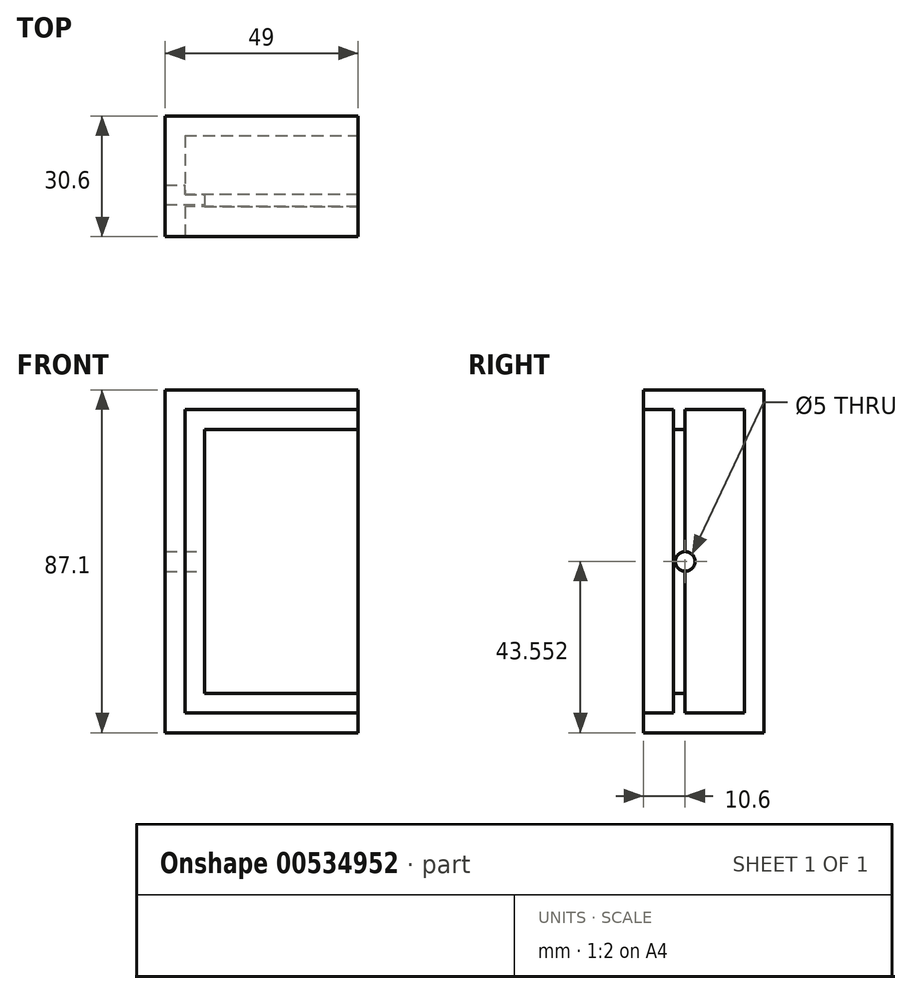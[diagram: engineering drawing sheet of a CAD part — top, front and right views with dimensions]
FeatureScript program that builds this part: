
annotation { "Feature Type Name" : "Feature", "Feature Type Description" : "" }
export const myFeature = defineFeature(function(context is Context, id is Id, definition is map)
    precondition{}
    {
        {
            var Q0;
            Q0=qCreatedBy(makeId("Front.planeOp"),FACE);
            var sketch = newSketch(context, id + "F0", { "sketchPlane" : qUnion([Q0])});
            skLineSegment(sketch, "E0.bottom", {"start": v(-22.43, 61.47) * mm, "end": v(21.57, 61.47) * mm});
            skLineSegment(sketch, "E0.top", {"start": v(-22.43, -15.63) * mm, "end": v(21.57, -15.63) * mm});
            skLineSegment(sketch, "E0.left", {"start": v(-22.43, 61.47) * mm, "end": v(-22.43, -15.63) * mm});
            skLineSegment(sketch, "E0.right", {"start": v(21.57, 61.47) * mm, "end": v(21.57, -15.63) * mm});
            skSolve(sketch);
        }
        {
            var Q0;
            Q0 = qSketchRegion(id + "F0", true);
            extrude(context, id + "F1", {"entities" : qUnion([Q0]), "depth" : 5 * mm, "offsetDistance" : 25.4 * mm});
        }
        {
            var Q0;
            Q0=makeQuery(id+"F1.opExtrude","SWEPT_FACE",FACE,{"disambiguationData":[OSD([sQuery(id+"F0.wireOp",EDGE,"E0.left")])]});
            var sketch = newSketch(context, id + "F2", { "sketchPlane" : qUnion([Q0])});
            skLineSegment(sketch, "E1.bottom", {"start": v(0, 61.47) * mm, "end": v(27.6, 61.47) * mm});
            skLineSegment(sketch, "E1.top", {"start": v(0, -15.63) * mm, "end": v(27.6, -15.63) * mm});
            skLineSegment(sketch, "E1.left", {"start": v(0, 61.47) * mm, "end": v(0, -15.63) * mm});
            skLineSegment(sketch, "E1.right", {"start": v(27.6, 61.47) * mm, "end": v(27.6, -15.63) * mm});
            skSolve(sketch);
        }
        {
            var Q0;
            Q0 = qSketchRegion(id + "F2", true);
            extrude(context, id + "F3", {"entities" : qUnion([Q0]), "operationType" : NewBodyOperationType.ADD, "depth" : 5 * mm, "offsetDistance" : 25.4 * mm});
        }
        {
            var Q0;
            Q0=makeQuery(id+"F3.boolean.opBoolean","MERGE",FACE,{"derivedFrom":[makeQuery(id+"F1.opExtrude","SWEPT_FACE",FACE,{"disambiguationData":[OSD([sQuery(id+"F0.wireOp",EDGE,"E0.bottom")])]}),makeQuery(id+"F3.opExtrude","SWEPT_FACE",FACE,{"disambiguationData":[OSD([sQuery(id+"F2.wireOp",EDGE,"E1.bottom")])]})]});
            var sketch = newSketch(context, id + "F4", { "sketchPlane" : qUnion([Q0])});
            skLineSegment(sketch, "E2.bottom", {"start": v(-27.43, 0) * mm, "end": v(21.57, 0) * mm});
            skLineSegment(sketch, "E2.top", {"start": v(-27.43, -27.6) * mm, "end": v(21.57, -27.6) * mm});
            skLineSegment(sketch, "E2.left", {"start": v(-27.43, 0) * mm, "end": v(-27.43, -27.6) * mm});
            skLineSegment(sketch, "E2.right", {"start": v(21.57, 0) * mm, "end": v(21.57, -27.6) * mm});
            skSolve(sketch);
        }
        {
            var Q0;
            Q0 = qSketchRegion(id + "F4", true);
            extrude(context, id + "F5", {"entities" : qUnion([Q0]), "operationType" : NewBodyOperationType.ADD, "depth" : 5 * mm, "offsetDistance" : 25.4 * mm});
        }
        {
            var Q0;
            Q0=makeQuery(id+"F3.boolean.opBoolean","MERGE",FACE,{"derivedFrom":[makeQuery(id+"F1.opExtrude","SWEPT_FACE",FACE,{"disambiguationData":[OSD([sQuery(id+"F0.wireOp",EDGE,"E0.top")])]}),makeQuery(id+"F3.opExtrude","SWEPT_FACE",FACE,{"disambiguationData":[OSD([sQuery(id+"F2.wireOp",EDGE,"E1.top")])]})]});
            var sketch = newSketch(context, id + "F6", { "sketchPlane" : qUnion([Q0])});
            skLineSegment(sketch, "E3.bottom", {"start": v(-27.43, 0) * mm, "end": v(21.57, 0) * mm});
            skLineSegment(sketch, "E3.top", {"start": v(-27.43, 27.6) * mm, "end": v(21.57, 27.6) * mm});
            skLineSegment(sketch, "E3.left", {"start": v(-27.43, 0) * mm, "end": v(-27.43, 27.6) * mm});
            skLineSegment(sketch, "E3.right", {"start": v(21.57, 0) * mm, "end": v(21.57, 27.6) * mm});
            skSolve(sketch);
        }
        {
            var Q0;
            Q0 = qSketchRegion(id + "F6", true);
            extrude(context, id + "F7", {"entities" : qUnion([Q0]), "operationType" : NewBodyOperationType.ADD, "depth" : 5 * mm, "offsetDistance" : 25.4 * mm});
        }
        {
            var Q0;
            Q0=makeQuery(id+"F5.opExtrude","CAP_FACE",FACE,{"disambiguationData":[OSD([sQuery(id+"F4.wireOp",EDGE,"E2.bottom"),sQuery(id+"F4.wireOp",EDGE,"E2.top"),sQuery(id+"F4.wireOp",EDGE,"E2.left"),sQuery(id+"F4.wireOp",EDGE,"E2.right")])],"isStart":true});
            var sketch = newSketch(context, id + "F8", { "sketchPlane" : qUnion([Q0])});
            skLineSegment(sketch, "E4", {"start": v(21.57, 27.6) * mm, "end": v(21.57, 20) * mm});
            skLineSegment(sketch, "E5", {"start": v(21.57, 20) * mm, "end": v(21.57, 5) * mm});
            skLineSegment(sketch, "E6.bottom", {"start": v(21.57, 20) * mm, "end": v(-22.43, 20) * mm});
            skLineSegment(sketch, "E6.top", {"start": v(21.57, 23) * mm, "end": v(-22.43, 23) * mm});
            skLineSegment(sketch, "E6.left", {"start": v(21.57, 20) * mm, "end": v(21.57, 23) * mm});
            skLineSegment(sketch, "E6.right", {"start": v(-22.43, 20) * mm, "end": v(-22.43, 23) * mm});
            skSolve(sketch);
        }
        {
            var Q0;
            Q0 = qSketchRegion(id + "F8", true);
            extrude(context, id + "F9", {"entities" : qUnion([Q0]), "operationType" : NewBodyOperationType.ADD, "depth" : 5 * mm, "offsetDistance" : 25.4 * mm});
        }
        {
            var Q0;
            Q0=makeQuery(id+"F3.opExtrude","CAP_FACE",FACE,{"disambiguationData":[OSD([sQuery(id+"F2.wireOp",EDGE,"E1.bottom"),sQuery(id+"F2.wireOp",EDGE,"E1.top"),sQuery(id+"F2.wireOp",EDGE,"E1.left"),sQuery(id+"F2.wireOp",EDGE,"E1.right")])],"isStart":true});
            var sketch = newSketch(context, id + "F10", { "sketchPlane" : qUnion([Q0])});
            skLineSegment(sketch, "E7.bottom", {"start": v(-23, 56.47) * mm, "end": v(-20, 56.47) * mm});
            skLineSegment(sketch, "E7.top", {"start": v(-23, -15.63) * mm, "end": v(-20, -15.63) * mm});
            skLineSegment(sketch, "E7.left", {"start": v(-23, 56.47) * mm, "end": v(-23, -15.63) * mm});
            skLineSegment(sketch, "E7.right", {"start": v(-20, 56.47) * mm, "end": v(-20, -15.63) * mm});
            skSolve(sketch);
        }
        {
            var Q0;
            Q0 = qSketchRegion(id + "F10", true);
            extrude(context, id + "F11", {"entities" : qUnion([Q0]), "operationType" : NewBodyOperationType.ADD, "depth" : 5 * mm, "offsetDistance" : 25.4 * mm});
        }
        {
            var Q0;
            Q0=makeQuery(id+"F7.opExtrude","CAP_FACE",FACE,{"disambiguationData":[OSD([sQuery(id+"F6.wireOp",EDGE,"E3.bottom"),sQuery(id+"F6.wireOp",EDGE,"E3.top"),sQuery(id+"F6.wireOp",EDGE,"E3.left"),sQuery(id+"F6.wireOp",EDGE,"E3.right")])],"isStart":true});
            var sketch = newSketch(context, id + "F12", { "sketchPlane" : qUnion([Q0])});
            skPoint(sketch, "E8.oppositeSnap0", {"position": v(21.57, -16.3) * mm});
            skLineSegment(sketch, "E8.bottom", {"start": v(-17.43, -23) * mm, "end": v(21.57, -23) * mm});
            skLineSegment(sketch, "E8.top", {"start": v(-17.43, -20) * mm, "end": v(21.57, -20) * mm});
            skLineSegment(sketch, "E8.left", {"start": v(-17.43, -23) * mm, "end": v(-17.43, -20) * mm});
            skLineSegment(sketch, "E8.right", {"start": v(21.57, -23) * mm, "end": v(21.57, -20) * mm});
            skSolve(sketch);
        }
        {
            var Q0;
            Q0 = qSketchRegion(id + "F12", true);
            extrude(context, id + "F13", {"entities" : qUnion([Q0]), "operationType" : NewBodyOperationType.ADD, "depth" : 5 * mm, "offsetDistance" : 25.4 * mm});
        }
        {
            var Q0;
            Q0=makeQuery(id+"F7.boolean.opBoolean","MERGE",FACE,{"derivedFrom":[makeQuery(id+"F5.boolean.opBoolean","MERGE",FACE,{"derivedFrom":[makeQuery(id+"F3.opExtrude","SWEPT_FACE",FACE,{"disambiguationData":[OSD([sQuery(id+"F2.wireOp",EDGE,"E1.right")])]}),makeQuery(id+"F5.opExtrude","SWEPT_FACE",FACE,{"disambiguationData":[OSD([sQuery(id+"F4.wireOp",EDGE,"E2.top")])]})]}),makeQuery(id+"F7.opExtrude","SWEPT_FACE",FACE,{"disambiguationData":[OSD([sQuery(id+"F6.wireOp",EDGE,"E3.top")])]})]});
            var sketch = newSketch(context, id + "F14", { "sketchPlane" : qUnion([Q0])});
            skLineSegment(sketch, "E9.bottom", {"start": v(21.57, -20.63) * mm, "end": v(-27.43, -20.63) * mm});
            skLineSegment(sketch, "E9.top", {"start": v(21.57, -15.63) * mm, "end": v(-27.43, -15.63) * mm});
            skLineSegment(sketch, "E9.left", {"start": v(21.57, -20.63) * mm, "end": v(21.57, -15.63) * mm});
            skLineSegment(sketch, "E9.right", {"start": v(-27.43, -20.63) * mm, "end": v(-27.43, -15.63) * mm});
            skLineSegment(sketch, "E10.bottom", {"start": v(-27.43, -15.63) * mm, "end": v(-22.43, -15.63) * mm});
            skLineSegment(sketch, "E10.top", {"start": v(-27.43, 66.47) * mm, "end": v(-22.43, 66.47) * mm});
            skLineSegment(sketch, "E10.left", {"start": v(-27.43, -15.63) * mm, "end": v(-27.43, 66.47) * mm});
            skLineSegment(sketch, "E10.right", {"start": v(-22.43, -15.63) * mm, "end": v(-22.43, 66.47) * mm});
            skLineSegment(sketch, "E11.bottom", {"start": v(-22.43, 66.47) * mm, "end": v(21.57, 66.47) * mm});
            skLineSegment(sketch, "E11.top", {"start": v(-22.43, 61.47) * mm, "end": v(21.57, 61.47) * mm});
            skLineSegment(sketch, "E11.left", {"start": v(-22.43, 66.47) * mm, "end": v(-22.43, 61.47) * mm});
            skLineSegment(sketch, "E11.right", {"start": v(21.57, 66.47) * mm, "end": v(21.57, 61.47) * mm});
            skSolve(sketch);
        }
        {
            var Q0;
            Q0 = qSketchRegion(id + "F14", true);
            extrude(context, id + "F15", {"entities" : qUnion([Q0]), "operationType" : NewBodyOperationType.ADD, "depth" : 3 * mm, "offsetDistance" : 25.4 * mm});
        }
        {
            var Q0;
            Q0=makeQuery(id+"F11.boolean.opBoolean","SPLIT",FACE,{"disambiguationData":[TD([makeQuery(id+"F9.opExtrude","SWEPT_FACE",FACE,{"disambiguationData":[OSD([sQuery(id+"F8.wireOp",EDGE,"E6.bottom")])]})])],"derivedFrom":makeQuery(id+"F3.opExtrude","CAP_FACE",FACE,{"disambiguationData":[OSD([sQuery(id+"F2.wireOp",EDGE,"E1.bottom"),sQuery(id+"F2.wireOp",EDGE,"E1.top"),sQuery(id+"F2.wireOp",EDGE,"E1.left"),sQuery(id+"F2.wireOp",EDGE,"E1.right")])],"isStart":true})});
            var sketch = newSketch(context, id + "F16", { "sketchPlane" : qUnion([Q0])});
            skCircle(sketch, "E12", {"center": v(-20, 22.92) * mm, "radius": 2.5 * mm});
            skSolve(sketch);
        }
        {
            var Q0;
            Q0 = qSketchRegion(id + "F16", true);
            extrude(context, id + "F17", {"entities" : qUnion([Q0]), "operationType" : NewBodyOperationType.REMOVE, "endBound" : BoundingType.SYMMETRIC, "oppositeDirection" : true, "depth" : 25.4 * mm, "offsetDistance" : 25.4 * mm});
        }
    });
